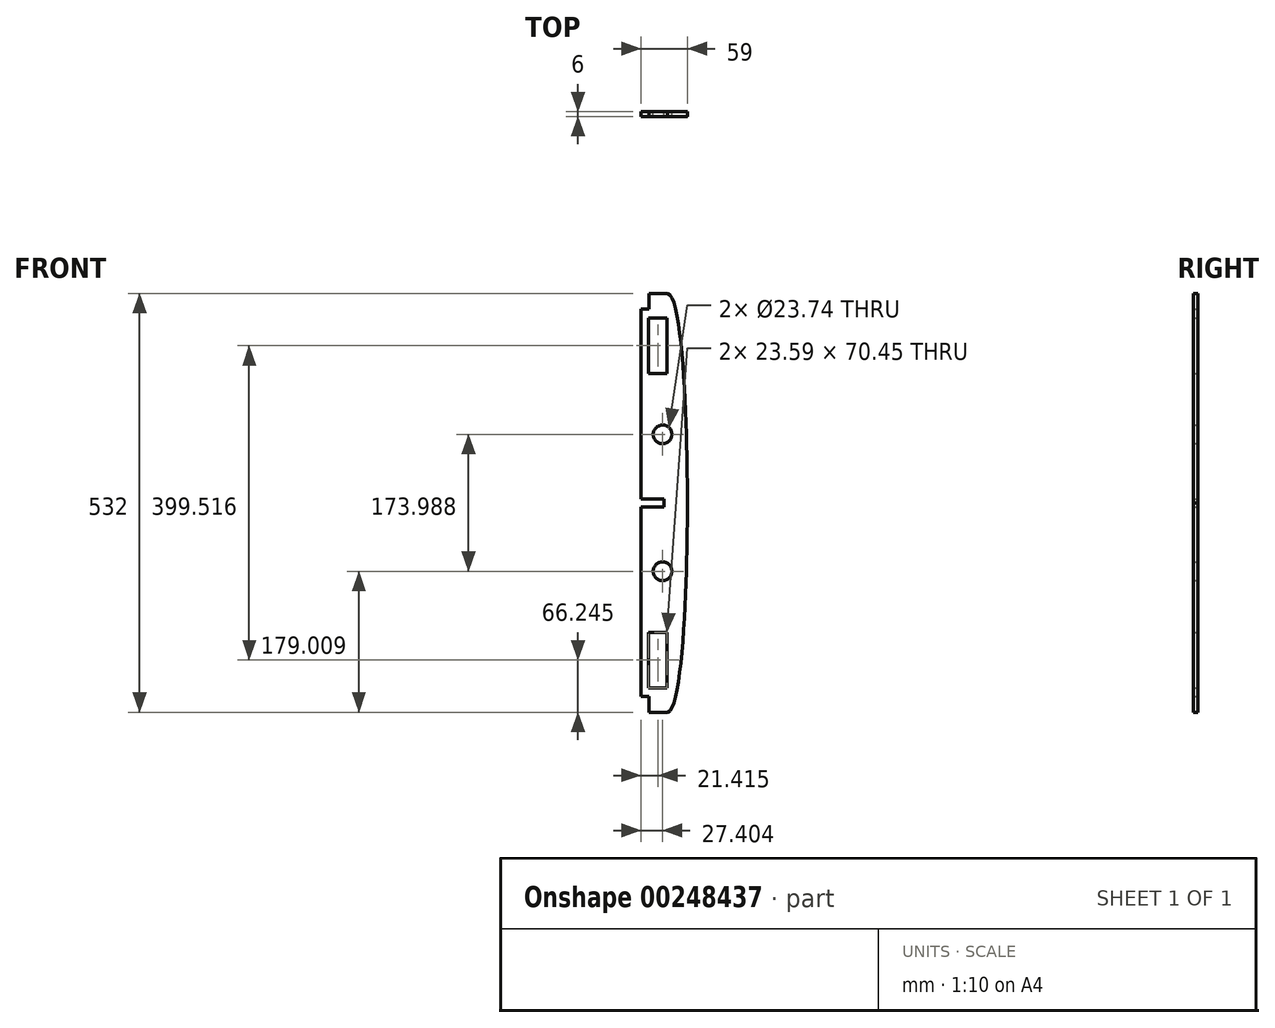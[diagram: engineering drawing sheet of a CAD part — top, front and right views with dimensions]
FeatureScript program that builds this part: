
annotation { "Feature Type Name" : "Feature", "Feature Type Description" : "" }
export const myFeature = defineFeature(function(context is Context, id is Id, definition is map)
    precondition{}
    {
        {
            var Q0;
            Q0=qCreatedBy(makeId("Front.planeOp"),FACE);
            var sketch = newSketch(context, id + "F0", { "sketchPlane" : qUnion([Q0])});
            skFitSpline(sketch, "E0", {"points": [v(586.66, 122.7) * mm, v(611.66, -143.3) * mm], "startDerivative": vector(74.82, -24) * mm, "endDerivative": vector(0.18, -7.65) * mm});
            skLineSegment(sketch, "E1", {"start": v(611.66, -143.3) * mm, "end": v(552.66, -143.3) * mm});
            skLineSegment(sketch, "E2", {"start": v(611.6, 122.7) * mm, "end": v(611.6, -140.76) * mm});
            skLineSegment(sketch, "E3.bottom", {"start": v(585.87, 91.68) * mm, "end": v(562.28, 91.68) * mm});
            skLineSegment(sketch, "E3.top", {"start": v(585.87, 21.23) * mm, "end": v(562.28, 21.23) * mm});
            skLineSegment(sketch, "E3.left", {"start": v(585.87, 91.68) * mm, "end": v(585.87, 21.23) * mm});
            skLineSegment(sketch, "E3.right", {"start": v(562.28, 91.68) * mm, "end": v(562.28, 21.23) * mm});
            skCircle(sketch, "E4", {"center": v(580.06, -56.31) * mm, "radius": 11.87 * mm});
            skLineSegment(sketch, "E5.MirrorCS", {"start": v(585.87, -378.3) * mm, "end": v(585.87, -307.84) * mm});
            skCircle(sketch, "E6.MirrorC", {"center": v(580.06, -230.3) * mm, "radius": 11.87 * mm});
            skLineSegment(sketch, "E7.MirrorCS", {"start": v(611.6, -409.3) * mm, "end": v(611.6, -145.86) * mm});
            skLineSegment(sketch, "E8.MirrorCS", {"start": v(562.28, -378.3) * mm, "end": v(562.28, -307.84) * mm});
            skFitSpline(sketch, "E9.MirrorCS", {"points": [v(586.66, -409.3) * mm, v(611.66, -143.3) * mm], "startDerivative": vector(74.82, 24) * mm, "endDerivative": vector(0.18, 7.65) * mm});
            skLineSegment(sketch, "E10.MirrorCS", {"start": v(585.87, -378.3) * mm, "end": v(562.28, -378.3) * mm});
            skLineSegment(sketch, "E11.MirrorCS", {"start": v(585.87, -307.84) * mm, "end": v(562.28, -307.84) * mm});
            skLineSegment(sketch, "E12", {"start": v(582.16, -143.3) * mm, "end": v(582.16, -148.3) * mm});
            skLineSegment(sketch, "E13", {"start": v(582.16, -143.3) * mm, "end": v(582.16, -138.3) * mm});
            skLineSegment(sketch, "E14", {"start": v(582.16, -138.3) * mm, "end": v(552.66, -138.3) * mm});
            skLineSegment(sketch, "E15", {"start": v(582.16, -148.3) * mm, "end": v(552.66, -148.3) * mm});
            skLineSegment(sketch, "E16", {"start": v(562.66, 122.7) * mm, "end": v(562.66, 102.7) * mm});
            skLineSegment(sketch, "E17", {"start": v(562.66, 102.7) * mm, "end": v(552.66, 102.7) * mm});
            skLineSegment(sketch, "E18", {"start": v(552.66, 102.7) * mm, "end": v(552.66, -143.3) * mm});
            skLineSegment(sketch, "E19", {"start": v(586.66, 122.7) * mm, "end": v(611.6, 122.7) * mm});
            skLineSegment(sketch, "E20", {"start": v(586.66, 122.7) * mm, "end": v(562.66, 122.7) * mm});
            skLineSegment(sketch, "E21.MirrorCS", {"start": v(562.66, -409.3) * mm, "end": v(562.66, -409.3) * mm});
            skLineSegment(sketch, "E22.MirrorCS", {"start": v(562.66, -389.3) * mm, "end": v(552.66, -389.3) * mm});
            skLineSegment(sketch, "E23", {"start": v(562.66, -409.3) * mm, "end": v(562.66, -389.3) * mm});
            skLineSegment(sketch, "E24", {"start": v(552.66, -389.3) * mm, "end": v(552.66, -143.3) * mm});
            skLineSegment(sketch, "E25", {"start": v(562.66, -409.3) * mm, "end": v(611.6, -409.3) * mm});
            skSolve(sketch);
        }
        {
            var Q0;
            {var subQ3=sQuery(id+"F0.wireOp",EDGE,"e4a9ef9c-881f-46ef-b2bc-2d1898208d58");Q0=makeQuery(id+"F0.imprint","IMPRINT",FACE,{"disambiguationData":[TD([[makeQuery(id+"F0.imprint","IMPRINT",EDGE,{"derivedFrom":subQ3}),-1.0]])]});}
            var Q1;
            Q1=makeQuery(id+"F0.imprint","IMPRINT",FACE,{"disambiguationData":[TD([[makeQuery(id+"F0.imprint","IMPRINT",EDGE,{"derivedFrom":sQuery(id+"F0.wireOp",EDGE,"E5.MirrorCS")}),-1.0]])]});
            var Q2;
            Q2=makeQuery(id+"F0.imprint","IMPRINT",FACE,{"disambiguationData":[TD([[makeQuery(id+"F0.imprint","IMPRINT",EDGE,{"derivedFrom":sQuery(id+"F0.wireOp",EDGE,"E3.bottom")}),-1.0]])]});
            extrude(context, id + "F1", {"entities" : qUnion([Q0, Q1, Q2]), "depth" : 6 * mm});
        }
    });
